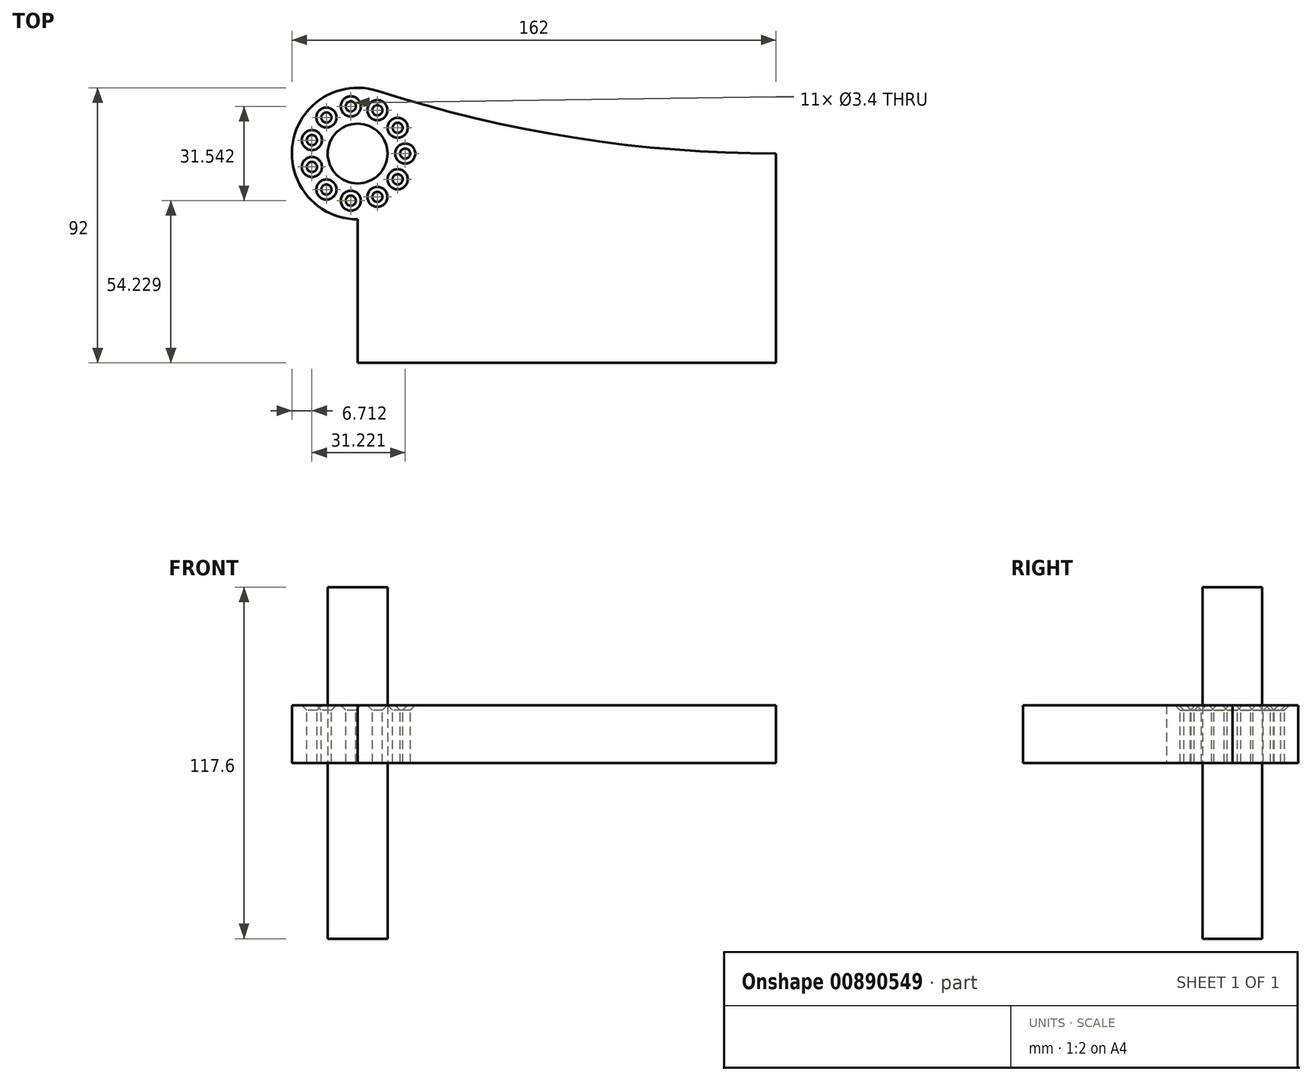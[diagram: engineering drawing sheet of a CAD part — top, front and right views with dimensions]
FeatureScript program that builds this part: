
annotation { "Feature Type Name" : "Feature", "Feature Type Description" : "" }
export const myFeature = defineFeature(function(context is Context, id is Id, definition is map)
    precondition{}
    {
        {
            var Q0;
            Q0=qCreatedBy(makeId("Top.planeOp"),FACE);
            var sketch = newSketch(context, id + "F0", { "sketchPlane" : qUnion([Q0])});
            skLineSegment(sketch, "E0.bottom", {"start": v(70, -35) * mm, "end": v(-70, -35) * mm});
            skLineSegment(sketch, "E0.top", {"start": v(70, 35) * mm, "end": v(-70, 35) * mm});
            skLineSegment(sketch, "E0.left", {"start": v(70, -35) * mm, "end": v(70, 35) * mm});
            skLineSegment(sketch, "E0.right", {"start": v(-70, -35) * mm, "end": v(-70, 35) * mm});
            skPoint(sketch, "E0.middle", {"position": v(0, 0) * mm});
            skCircle(sketch, "E1", {"center": v(-70, 35) * mm, "radius": 22 * mm});
            skArc(sketch, "E2", {"start": v(-63.25, 55.94) * mm, "mid": v(2.56, 40.27) * mm, "end": v(70, 35) * mm});
            skCircle(sketch, "E3", {"center": v(-70, 35) * mm, "radius": 10 * mm});
            skSolve(sketch);
        }
        {
            var Q0;
            {var subQ0=sQuery(id+"F0.wireOp",EDGE,"E1");var subQ4=sQuery(id+"F0.wireOp",EDGE,"E0.top");var subQ5=makeQuery(id+"F0.imprint","INTERSECT",VERTEX,{"derivedFrom":[subQ4,subQ0]});Q0=makeQuery(id+"F0.imprint","IMPRINT",FACE,{"disambiguationData":[TD([[makeQuery(id+"F0.imprint","IMPRINT",EDGE,{"disambiguationData":[TD([[subQ5,-1.0]])],"derivedFrom":subQ4}),-1.0]])]});}
            var Q1;
            {var subQ0=sQuery(id+"F0.wireOp",EDGE,"E2");Q1=makeQuery(id+"F0.imprint","IMPRINT",FACE,{"disambiguationData":[TD([[makeQuery(id+"F0.imprint","IMPRINT",EDGE,{"derivedFrom":subQ0}),-1.0]])]});}
            var Q2;
            {var subQ0=sQuery(id+"F0.wireOp",EDGE,"E1");var subQ1=sQuery(id+"F0.wireOp",EDGE,"E0.top");var subQ2=makeQuery(id+"F0.imprint","INTERSECT",VERTEX,{"derivedFrom":[subQ1,subQ0]});Q2=makeQuery(id+"F0.imprint","IMPRINT",FACE,{"disambiguationData":[TD([[makeQuery(id+"F0.imprint","IMPRINT",EDGE,{"disambiguationData":[TD([[subQ2,-1.0]])],"derivedFrom":subQ1}),1.0]])]});}
            var Q3;
            {var subQ5=sQuery(id+"F0.wireOp",EDGE,"E0.bottom");Q3=makeQuery(id+"F0.imprint","IMPRINT",FACE,{"disambiguationData":[TD([[makeQuery(id+"F0.imprint","IMPRINT",EDGE,{"derivedFrom":subQ5}),-1.0]])]});}
            extrude(context, id + "F1", {"entities" : qUnion([Q0, Q1, Q2, Q3]), "depth" : 19.3 * mm, "offsetDistance" : 25 * mm});
        }
        {
            var Q0;
            {var subQ0=sQuery(id+"F0.wireOp",EDGE,"E0.right");var subQ1=sQuery(id+"F0.wireOp",EDGE,"E0.top");var subQ2=makeQuery(id+"F0.imprint","INTERSECT",VERTEX,{"derivedFrom":[subQ1,subQ0]});Q0=makeQuery(id+"F0.imprint","IMPRINT",FACE,{"disambiguationData":[TD([[makeQuery(id+"F0.imprint","IMPRINT",EDGE,{"disambiguationData":[TD([[subQ2,1.0]])],"derivedFrom":subQ1}),-1.0]])]});}
            var Q1;
            {var subQ0=sQuery(id+"F0.wireOp",EDGE,"E0.right");var subQ1=sQuery(id+"F0.wireOp",EDGE,"E0.top");var subQ2=makeQuery(id+"F0.imprint","INTERSECT",VERTEX,{"derivedFrom":[subQ1,subQ0]});Q1=makeQuery(id+"F0.imprint","IMPRINT",FACE,{"disambiguationData":[TD([[makeQuery(id+"F0.imprint","IMPRINT",EDGE,{"disambiguationData":[TD([[subQ2,1.0]])],"derivedFrom":subQ1}),1.0]])]});}
            extrude(context, id + "F2", {"entities" : qUnion([Q0, Q1]), "depth" : 117.6 * mm, "offsetDistance" : 25 * mm, "symmetric" : true});
        }
        {
            var Q0;
            Q0=makeQuery(id+"F1.opExtrude","CAP_FACE",FACE,{"disambiguationData":[OSD([sQuery(id+"F0.wireOp",EDGE,"E0.bottom"),sQuery(id+"F0.wireOp",EDGE,"E0.left"),sQuery(id+"F0.wireOp",EDGE,"E0.right"),sQuery(id+"F0.wireOp",EDGE,"E1"),sQuery(id+"F0.wireOp",EDGE,"E2"),sQuery(id+"F0.wireOp",EDGE,"E3")])],"isStart":false});
            var sketch = newSketch(context, id + "F3", { "sketchPlane" : qUnion([Q0])});
            skLineSegment(sketch, "E4.0", {"start": v(70, 35) * mm, "end": v(-70, 35) * mm, "construction": true});
            skPoint(sketch, "E5", {"position": v(-54.07, 35) * mm});
            skPoint(sketch, "E6.1.0", {"position": v(-56.6, 43.61) * mm});
            skPoint(sketch, "E6.2.0", {"position": v(-63.38, 49.5) * mm});
            skPoint(sketch, "E6.3.0", {"position": v(-72.27, 50.77) * mm});
            skPoint(sketch, "E6.4.0", {"position": v(-80.43, 47.04) * mm});
            skPoint(sketch, "E6.5.0", {"position": v(-85.29, 39.49) * mm});
            skPoint(sketch, "E6.6.0", {"position": v(-85.29, 30.51) * mm});
            skPoint(sketch, "E6.7.0", {"position": v(-80.43, 22.96) * mm});
            skPoint(sketch, "E6.8.0", {"position": v(-72.27, 19.23) * mm});
            skPoint(sketch, "E6.9.0", {"position": v(-63.38, 20.5) * mm});
            skPoint(sketch, "E6.10.0", {"position": v(-56.6, 26.39) * mm});
            skPoint(sketch, "E6.center", {"position": v(-70, 35) * mm});
            skSolve(sketch);
        }
        {
            var Q0;
            Q0=sQuery(id+"F3.wireOp",VERTEX,"E6.3.0");
            var Q1;
            Q1=sQuery(id+"F3.wireOp",VERTEX,"E6.2.0");
            var Q2;
            Q2=sQuery(id+"F3.wireOp",VERTEX,"E6.1.0");
            var Q3;
            Q3=sQuery(id+"F3.wireOp",VERTEX,"E5");
            var Q4;
            Q4=sQuery(id+"F3.wireOp",VERTEX,"E6.10.0");
            var Q5;
            Q5=sQuery(id+"F3.wireOp",VERTEX,"E6.9.0");
            var Q6;
            Q6=sQuery(id+"F3.wireOp",VERTEX,"E6.8.0");
            var Q7;
            Q7=sQuery(id+"F3.wireOp",VERTEX,"E6.7.0");
            var Q8;
            Q8=sQuery(id+"F3.wireOp",VERTEX,"E6.6.0");
            var Q9;
            Q9=sQuery(id+"F3.wireOp",VERTEX,"E6.5.0");
            var Q10;
            Q10=sQuery(id+"F3.wireOp",VERTEX,"E6.4.0");
            var Q11;
            Q11=makeQuery(id+"F1.opExtrude","SWEPT_BODY",BODY,{"disambiguationData":[OSD([sQuery(id+"F0.wireOp",EDGE,"E0.bottom"),sQuery(id+"F0.wireOp",EDGE,"E0.left"),sQuery(id+"F0.wireOp",EDGE,"E0.right"),sQuery(id+"F0.wireOp",EDGE,"E1"),sQuery(id+"F0.wireOp",EDGE,"E2"),sQuery(id+"F0.wireOp",EDGE,"E3")])]});
            hole(context, id + "F4", {"style" : HoleStyle.C_SINK, "endStyle" : HoleEndStyle.THROUGH, "standardTappedOrClearance" : lookupTablePath({ "fit" : "Normal", "standard" : "ISO", "size" : "M3", "type" : "Clearance" }), "standardBlindInLast" : lookupTablePath({ "fit" : "Normal", "standard" : "ISO", "size" : "M3", "type" : "Clearance" }), "holeDiameter" : 3.4 * mm, "cSinkDiameter" : 6.72 * mm, "cSinkAngle" : 90 * degree, "majorDiameter" : 5 * mm, "isTappedThrough" : true, "tappedDepth" : 12 * mm, "tapClearance" : 3, "locations" : qUnion([Q0, Q1, Q2, Q3, Q4, Q5, Q6, Q7, Q8, Q9, Q10]), "scope" : qUnion([Q11])});
        }
    });
